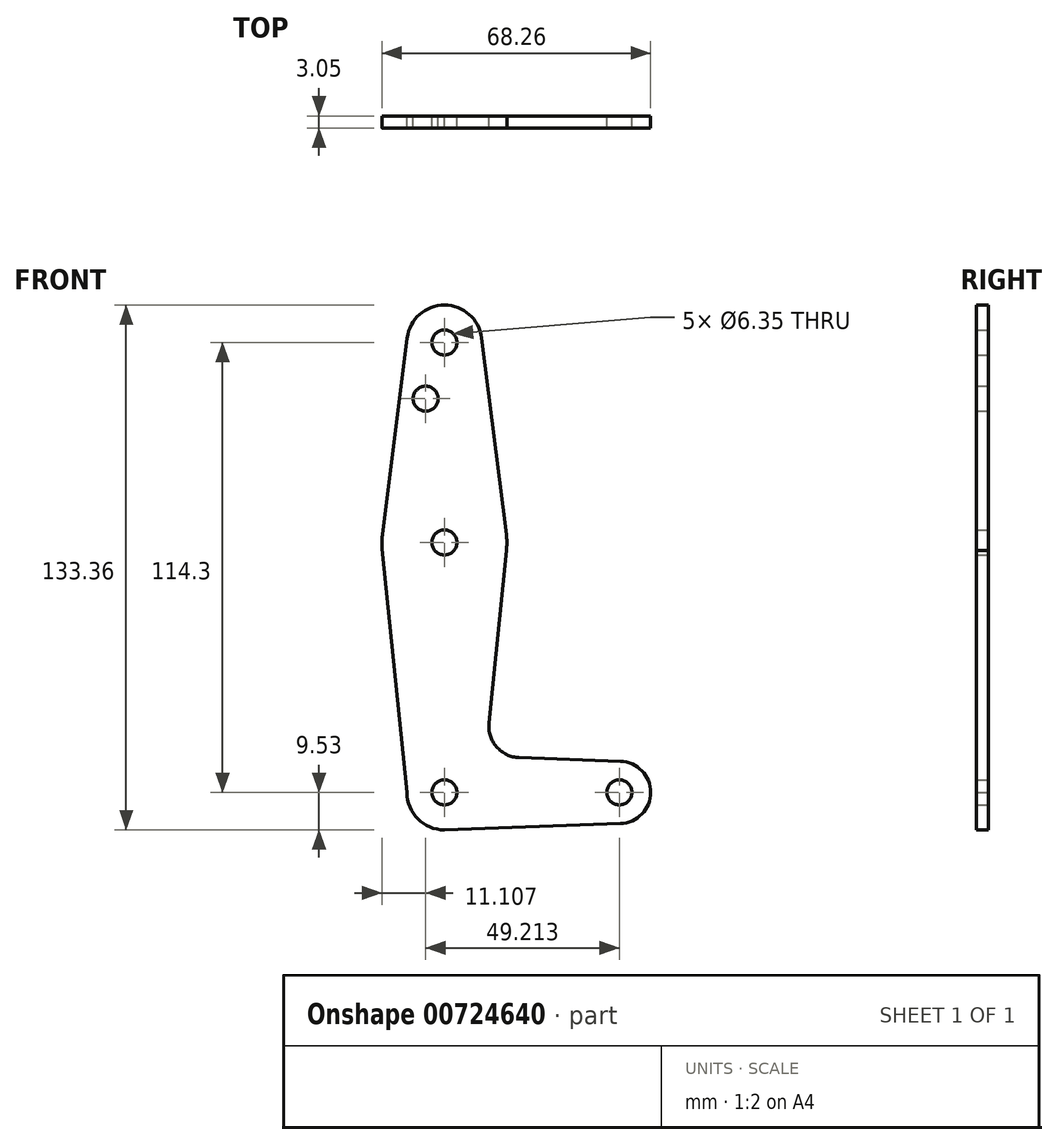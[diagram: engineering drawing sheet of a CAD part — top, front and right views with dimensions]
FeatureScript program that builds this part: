
annotation { "Feature Type Name" : "Feature", "Feature Type Description" : "" }
export const myFeature = defineFeature(function(context is Context, id is Id, definition is map)
    precondition{}
    {
        {
            var Q0;
            Q0=qCreatedBy(makeId("Front.planeOp"),FACE);
            var sketch = newSketch(context, id + "F0", { "sketchPlane" : qUnion([Q0])});
            skLineSegment(sketch, "E0", {"start": v(0, 0) * mm, "end": v(0, 114.3) * mm, "construction": true});
            skLineSegment(sketch, "E1", {"start": v(0, 0) * mm, "end": v(44.45, 0) * mm, "construction": true});
            skCircle(sketch, "E2", {"center": v(0, 114.3) * mm, "radius": 9.53 * mm});
            skCircle(sketch, "E3", {"center": v(0, 63.5) * mm, "radius": 15.88 * mm});
            skCircle(sketch, "E4", {"center": v(0, 0) * mm, "radius": 9.53 * mm});
            skCircle(sketch, "E5", {"center": v(44.45, 0) * mm, "radius": 7.94 * mm});
            skLineSegment(sketch, "E6", {"start": v(-9.45, 115.5) * mm, "end": v(-15.75, 65.48) * mm});
            skLineSegment(sketch, "E7", {"start": v(9.45, 115.5) * mm, "end": v(15.75, 65.48) * mm});
            skLineSegment(sketch, "E8", {"start": v(0, -9.53) * mm, "end": v(44.73, -7.93) * mm});
            skLineSegment(sketch, "E9", {"start": v(18.97, 8.85) * mm, "end": v(44.73, 7.93) * mm});
            skLineSegment(sketch, "E10", {"start": v(15.75, 61.52) * mm, "end": v(11.34, 17.59) * mm});
            skLineSegment(sketch, "E11", {"start": v(-9.52, 0) * mm, "end": v(-15.8, 61.9) * mm});
            skCircle(sketch, "E12", {"center": v(-4.76, 100.03) * mm, "radius": 3.18 * mm});
            skCircle(sketch, "E13", {"center": v(0, 63.5) * mm, "radius": 3.18 * mm});
            skCircle(sketch, "E14", {"center": v(0, 114.3) * mm, "radius": 3.18 * mm});
            skCircle(sketch, "E15", {"center": v(0, 0) * mm, "radius": 3.18 * mm});
            skCircle(sketch, "E16", {"center": v(44.45, 0) * mm, "radius": 3.18 * mm});
            skPoint(sketch, "E17.newPointA", {"position": v(9.57, 0) * mm});
            skArc(sketch, "E17.filletArc", {"start": v(11.34, 17.59) * mm, "mid": v(13.26, 11.57) * mm, "end": v(18.97, 8.85) * mm});
            skSolve(sketch);
        }
        {
            var Q0;
            {var subQ1=sQuery(id+"F0.wireOp",EDGE,"E6");Q0=makeQuery(id+"F0.imprint","IMPRINT",FACE,{"disambiguationData":[TD([[makeQuery(id+"F0.imprint","IMPRINT",EDGE,{"derivedFrom":subQ1}),1.0]])]});}
            var Q1;
            {var subQ6=sQuery(id+"F0.wireOp",EDGE,"E9");Q1=makeQuery(id+"F0.imprint","IMPRINT",FACE,{"disambiguationData":[TD([[makeQuery(id+"F0.imprint","IMPRINT",EDGE,{"derivedFrom":subQ6}),-1.0]])]});}
            var Q2;
            Q2=makeQuery(id+"F0.imprint","IMPRINT",FACE,{"disambiguationData":[TD([[makeQuery(id+"F0.imprint","IMPRINT",EDGE,{"derivedFrom":sQuery(id+"F0.wireOp",EDGE,"E13")}),-1.0]])]});
            var Q3;
            Q3=makeQuery(id+"F0.imprint","IMPRINT",FACE,{"disambiguationData":[TD([[makeQuery(id+"F0.imprint","IMPRINT",EDGE,{"derivedFrom":sQuery(id+"F0.wireOp",EDGE,"E15")}),-1.0]])]});
            var Q4;
            Q4=makeQuery(id+"F0.imprint","IMPRINT",FACE,{"disambiguationData":[TD([[makeQuery(id+"F0.imprint","IMPRINT",EDGE,{"derivedFrom":sQuery(id+"F0.wireOp",EDGE,"E16")}),-1.0]])]});
            var Q5;
            Q5=makeQuery(id+"F0.imprint","IMPRINT",FACE,{"disambiguationData":[TD([[makeQuery(id+"F0.imprint","IMPRINT",EDGE,{"derivedFrom":sQuery(id+"F0.wireOp",EDGE,"E14")}),-1.0]])]});
            extrude(context, id + "F1", {"entities" : qUnion([Q0, Q1, Q2, Q3, Q4, Q5]), "depth" : 3.05 * mm, "offsetDistance" : 25.4 * mm});
        }
    });
